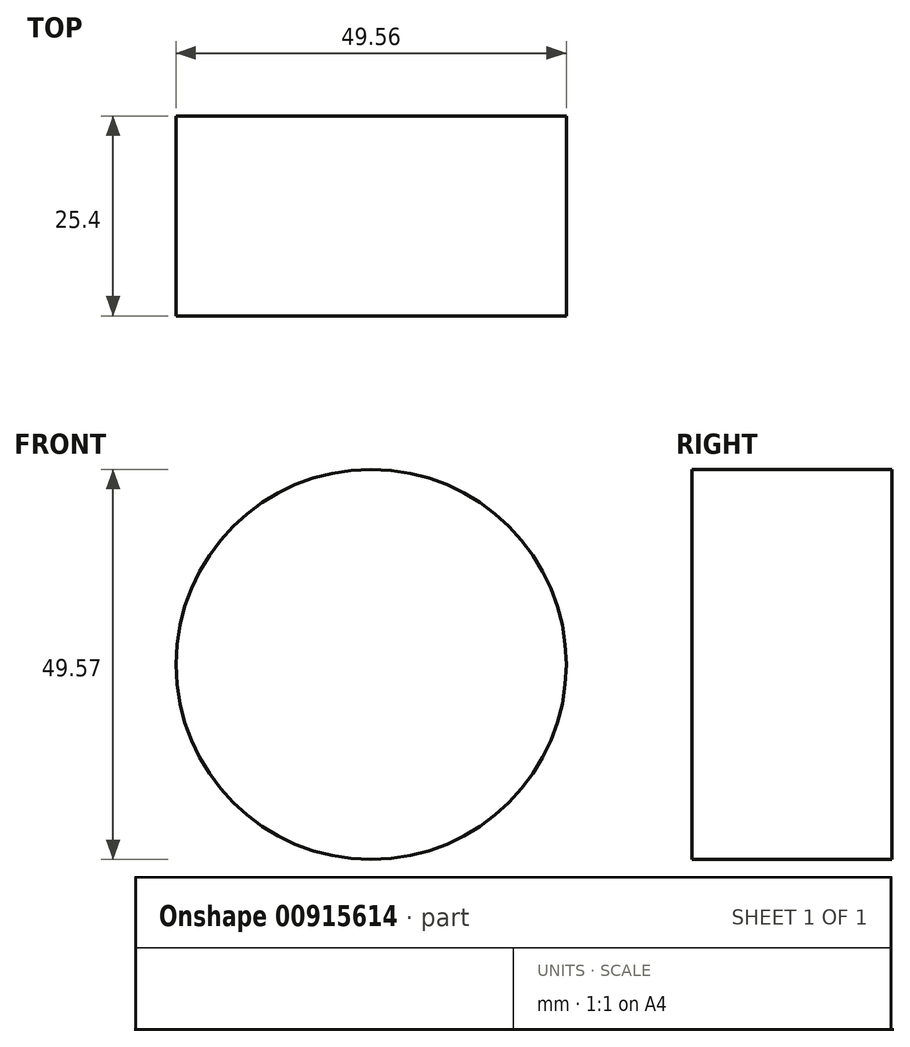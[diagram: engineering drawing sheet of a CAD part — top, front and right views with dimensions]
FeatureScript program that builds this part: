
annotation { "Feature Type Name" : "Feature", "Feature Type Description" : "" }
export const myFeature = defineFeature(function(context is Context, id is Id, definition is map)
    precondition{}
    {
        {
            var Q0;
            Q0=qCreatedBy(makeId("Front.planeOp"),FACE);
            var sketch = newSketch(context, id + "F0", { "sketchPlane" : qUnion([Q0])});
            skCircle(sketch, "E0", {"center": v(0.52, 0.07) * mm, "radius": 24.78 * mm});
            skSolve(sketch);
        }
        {
            var Q0;
            Q0 = qSketchRegion(id + "F0", true);
            var Q1;
            Q1=makeQuery(id+"F0.imprint","IMPRINT",FACE,{"disambiguationData":[TD([[makeQuery(id+"F0.imprint","IMPRINT",EDGE,{"derivedFrom":sQuery(id+"F0.wireOp",EDGE,"E0")}),1.0]])]});
            extrude(context, id + "F1", {"entities" : qUnion([Q0, Q1]), "depth" : 25.4 * mm, "offsetDistance" : 25.4 * mm});
        }
    });
